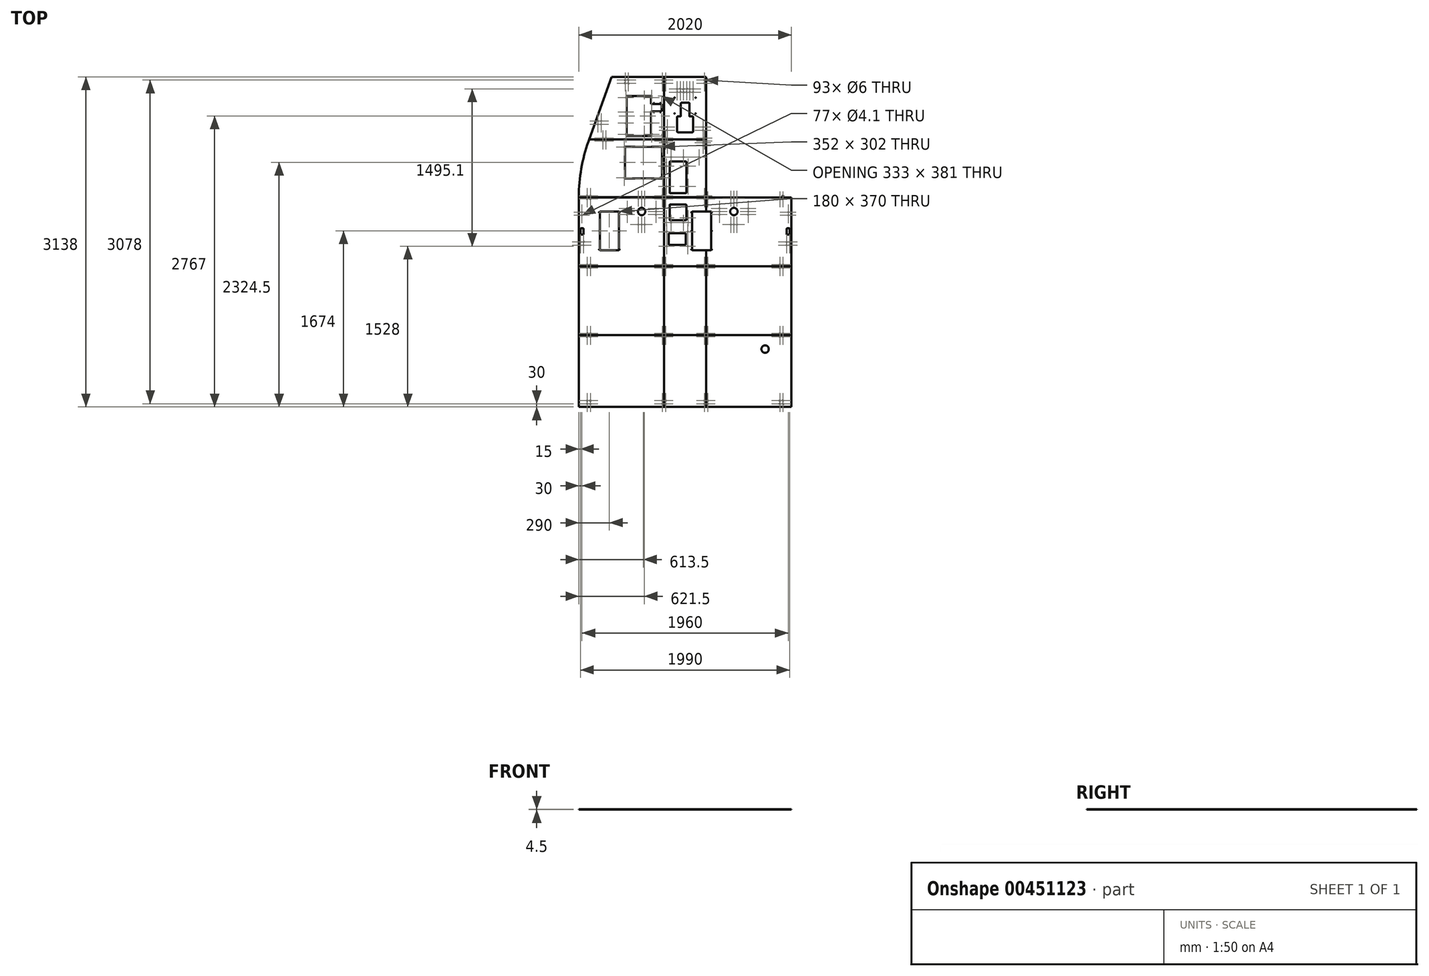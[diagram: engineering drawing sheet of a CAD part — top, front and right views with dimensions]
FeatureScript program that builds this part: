
annotation { "Feature Type Name" : "Feature", "Feature Type Description" : "" }
export const myFeature = defineFeature(function(context is Context, id is Id, definition is map)
    precondition{}
    {
        {
            var Q0;
            Q0=qCreatedBy(makeId("Top.planeOp"),FACE);
            var sketch = newSketch(context, id + "F0", { "sketchPlane" : qUnion([Q0])});
            skLineSegment(sketch, "E0.bottom", {"start": v(200, -327.5) * mm, "end": v(-200, -327.5) * mm});
            skLineSegment(sketch, "E0.top", {"start": v(200, 327.5) * mm, "end": v(-200, 327.5) * mm});
            skLineSegment(sketch, "E0.left", {"start": v(200, -327.5) * mm, "end": v(200, -176.5) * mm});
            skLineSegment(sketch, "E0.right", {"start": v(-200, -327.5) * mm, "end": v(-200, 327.5) * mm});
            skPoint(sketch, "E0.middle", {"position": v(0, 0) * mm});
            skCircle(sketch, "E1", {"center": v(185, 312.5) * mm, "radius": 3 * mm});
            skCircle(sketch, "E2", {"center": v(-185, 312.5) * mm, "radius": 3 * mm});
            skLineSegment(sketch, "E3.bottom", {"start": v(12.5, 109) * mm, "end": v(-147.5, 109) * mm});
            skLineSegment(sketch, "E3.top", {"start": v(12.5, 259) * mm, "end": v(-147.5, 259) * mm});
            skLineSegment(sketch, "E3.left", {"start": v(12.5, 109) * mm, "end": v(12.5, 259) * mm});
            skLineSegment(sketch, "E3.right", {"start": v(-147.5, 109) * mm, "end": v(-147.5, 259) * mm});
            skPoint(sketch, "E3.middle", {"position": v(-67.5, 184) * mm});
            skCircle(sketch, "E4", {"center": v(-134.5, 86.5) * mm, "radius": 2.05 * mm});
            skCircle(sketch, "E5", {"center": v(-17.5, 86.5) * mm, "radius": 2.05 * mm});
            skCircle(sketch, "E6", {"center": v(27.5, 131.5) * mm, "radius": 2.05 * mm});
            skCircle(sketch, "E7", {"center": v(-185, -312.5) * mm, "radius": 3 * mm});
            skCircle(sketch, "E8", {"center": v(185, -312.5) * mm, "radius": 3 * mm});
            skCircle(sketch, "E9", {"center": v(61, 185.5) * mm, "radius": 2.5 * mm});
            skCircle(sketch, "E10", {"center": v(61, 8.5) * mm, "radius": 2.5 * mm});
            skCircle(sketch, "E11", {"center": v(61, -168.5) * mm, "radius": 2.5 * mm});
            skLineSegment(sketch, "E12.bottom", {"start": v(200, -176.5) * mm, "end": v(67, -176.5) * mm});
            skLineSegment(sketch, "E12.top", {"start": v(200, 193.5) * mm, "end": v(67, 193.5) * mm});
            skLineSegment(sketch, "E12.right", {"start": v(67, -176.5) * mm, "end": v(67, 193.5) * mm});
            skPoint(sketch, "E12.middle", {"position": v(133.5, 8.5) * mm});
            skLineSegment(sketch, "E13.trimOffspring", {"start": v(200, 193.5) * mm, "end": v(200, 327.5) * mm});
            skLineSegment(sketch, "E14.bottom", {"start": v(5, -123.5) * mm, "end": v(-155, -123.5) * mm});
            skLineSegment(sketch, "E14.top", {"start": v(5, -13.5) * mm, "end": v(-155, -13.5) * mm});
            skLineSegment(sketch, "E14.left", {"start": v(5, -123.5) * mm, "end": v(5, -13.5) * mm});
            skLineSegment(sketch, "E14.right", {"start": v(-155, -123.5) * mm, "end": v(-155, -13.5) * mm});
            skPoint(sketch, "E14.middle", {"position": v(-75, -68.5) * mm});
            skCircle(sketch, "E15", {"center": v(-175, 0.5) * mm, "radius": 2.05 * mm});
            skCircle(sketch, "E16", {"center": v(-175, -137.5) * mm, "radius": 2.05 * mm});
            skCircle(sketch, "E17", {"center": v(25, 0.5) * mm, "radius": 2.05 * mm});
            skCircle(sketch, "E18", {"center": v(25, -137.5) * mm, "radius": 2.05 * mm});
            skCircle(sketch, "E19", {"center": v(-177.5, 131.5) * mm, "radius": 2.05 * mm});
            skSolve(sketch);
        }
        {
            var Q0;
            Q0=qSketchRegion(id+"F0",true);
            extrude(context, id + "F1", {"entities" : qUnion([Q0]), "depth" : 4.5 * mm, "offsetDistance" : 25 * mm});
        }
        {
            var Q0;
            Q0=qCreatedBy(makeId("Top.planeOp"),FACE);
            var sketch = newSketch(context, id + "F2", { "sketchPlane" : qUnion([Q0])});
            skLineSegment(sketch, "E20.top", {"start": v(-200, 877.5) * mm, "end": v(-912, 877.5) * mm});
            skLineSegment(sketch, "E20.left", {"start": v(-200, 327.5) * mm, "end": v(-200, 877.5) * mm});
            skPoint(sketch, "E20.middle", {"position": v(-556, 602.5) * mm});
            skLineSegment(sketch, "E21", {"start": v(-200, 327.5) * mm, "end": v(-1010, 327.5) * mm});
            skCircle(sketch, "E22", {"center": v(-215, 862.5) * mm, "radius": 3 * mm});
            skCircle(sketch, "E23", {"center": v(-215, 342.5) * mm, "radius": 3 * mm});
            skCircle(sketch, "E24", {"center": v(-930, 342.5) * mm, "radius": 3 * mm});
            skCircle(sketch, "E25", {"center": v(-782, 862.5) * mm, "radius": 3 * mm});
            skLineSegment(sketch, "E26.left", {"start": v(-200, 877.5) * mm, "end": v(-200, 1472.5) * mm});
            skPoint(sketch, "E26.middle", {"position": v(-556, 1175) * mm});
            skLineSegment(sketch, "E27", {"start": v(-200, 1472.5) * mm, "end": v(-700, 1472.5) * mm});
            skLineSegment(sketch, "E28", {"start": v(-912, 877.5) * mm, "end": v(-700, 1472.5) * mm});
            skCircle(sketch, "E29", {"center": v(-215, 1442.5) * mm, "radius": 3 * mm});
            skCircle(sketch, "E30", {"center": v(-215, 892.5) * mm, "radius": 3 * mm});
            skCircle(sketch, "E31", {"center": v(-782, 892.5) * mm, "radius": 3 * mm});
            skCircle(sketch, "E32", {"center": v(-570, 1442.5) * mm, "radius": 3 * mm});
            skLineSegment(sketch, "E33", {"start": v(0, 1490.85) * mm, "end": v(0, 501.43) * mm, "construction": true});
            skCircle(sketch, "E34.MirrorC", {"center": v(215, 1442.5) * mm, "radius": 3 * mm});
            skCircle(sketch, "E35.MirrorC", {"center": v(930, 342.5) * mm, "radius": 3 * mm});
            skCircle(sketch, "E36.MirrorC", {"center": v(782, 862.5) * mm, "radius": 3 * mm});
            skCircle(sketch, "E37.MirrorC", {"center": v(782, 892.5) * mm, "radius": 3 * mm});
            skCircle(sketch, "E38.MirrorC", {"center": v(570, 1442.5) * mm, "radius": 3 * mm});
            skCircle(sketch, "E39.MirrorC", {"center": v(215, 862.5) * mm, "radius": 3 * mm});
            skCircle(sketch, "E40.MirrorC", {"center": v(215, 342.5) * mm, "radius": 3 * mm});
            skCircle(sketch, "E41.MirrorC", {"center": v(215, 892.5) * mm, "radius": 3 * mm});
            skLineSegment(sketch, "E42.MirrorCS", {"start": v(200, 1472.5) * mm, "end": v(700, 1472.5) * mm});
            skLineSegment(sketch, "E43.MirrorCS", {"start": v(1010, 327.5) * mm, "end": v(912, 877.5) * mm, "construction": true});
            skLineSegment(sketch, "E44.MirrorCS", {"start": v(200, 877.5) * mm, "end": v(912, 877.5) * mm});
            skPoint(sketch, "E45.MirrorP", {"position": v(556, 1175) * mm});
            skLineSegment(sketch, "E46.MirrorCS", {"start": v(200, 327.5) * mm, "end": v(200, 877.5) * mm});
            skPoint(sketch, "E47.MirrorP", {"position": v(556, 602.5) * mm});
            skLineSegment(sketch, "E48.MirrorCS", {"start": v(200, 327.5) * mm, "end": v(1010, 327.5) * mm});
            skLineSegment(sketch, "E49.MirrorCS", {"start": v(912, 877.5) * mm, "end": v(700, 1472.5) * mm});
            skLineSegment(sketch, "E50.MirrorCS", {"start": v(200, 877.5) * mm, "end": v(200, 1472.5) * mm});
            skCircle(sketch, "E51", {"center": v(-900, 342.5) * mm, "radius": 3 * mm});
            skCircle(sketch, "E52", {"center": v(-752, 862.5) * mm, "radius": 3 * mm});
            skCircle(sketch, "E53", {"center": v(-752, 892.5) * mm, "radius": 3 * mm});
            skCircle(sketch, "E54", {"center": v(-570, 1412.5) * mm, "radius": 3 * mm});
            skCircle(sketch, "E55", {"center": v(-540, 1442.5) * mm, "radius": 3 * mm});
            skCircle(sketch, "E56", {"center": v(-540, 1412.5) * mm, "radius": 3 * mm});
            skCircle(sketch, "E57", {"center": v(-215, 1412.5) * mm, "radius": 3 * mm});
            skCircle(sketch, "E58.MirrorC", {"center": v(215, 1412.5) * mm, "radius": 3 * mm});
            skCircle(sketch, "E59.MirrorC", {"center": v(540, 1442.5) * mm, "radius": 3 * mm});
            skCircle(sketch, "E60.MirrorC", {"center": v(540, 1412.5) * mm, "radius": 3 * mm});
            skCircle(sketch, "E61.MirrorC", {"center": v(570, 1412.5) * mm, "radius": 3 * mm});
            skCircle(sketch, "E62.MirrorC", {"center": v(752, 892.5) * mm, "radius": 3 * mm});
            skCircle(sketch, "E63.MirrorC", {"center": v(752, 862.5) * mm, "radius": 3 * mm});
            skCircle(sketch, "E64.MirrorC", {"center": v(900, 342.5) * mm, "radius": 3 * mm});
            skCircle(sketch, "E65", {"center": v(-828.5, 1052.5) * mm, "radius": 2.05 * mm});
            skCircle(sketch, "E66", {"center": v(-798.5, 1052.5) * mm, "radius": 2.05 * mm});
            skCircle(sketch, "E67", {"center": v(-828.5, 1022.5) * mm, "radius": 2.05 * mm});
            skCircle(sketch, "E68", {"center": v(-798.5, 1022.5) * mm, "radius": 2.05 * mm});
            skCircle(sketch, "E69.MirrorC", {"center": v(828.5, 1022.5) * mm, "radius": 2.05 * mm});
            skCircle(sketch, "E70.MirrorC", {"center": v(798.5, 1052.5) * mm, "radius": 2.05 * mm});
            skCircle(sketch, "E71.MirrorC", {"center": v(828.5, 1052.5) * mm, "radius": 2.05 * mm});
            skCircle(sketch, "E72.MirrorC", {"center": v(798.5, 1022.5) * mm, "radius": 2.05 * mm});
            skCircle(sketch, "E73", {"center": v(-443.5, 383.5) * mm, "radius": 2.05 * mm, "construction": true});
            skCircle(sketch, "E74", {"center": v(-413.5, 383.5) * mm, "radius": 2.05 * mm, "construction": true});
            skCircle(sketch, "E75", {"center": v(-383.5, 383.5) * mm, "radius": 2.05 * mm, "construction": true});
            skCircle(sketch, "E76", {"center": v(433.5, 383.5) * mm, "radius": 2.05 * mm, "construction": true});
            skCircle(sketch, "E77", {"center": v(463.5, 383.5) * mm, "radius": 2.05 * mm, "construction": true});
            skCircle(sketch, "E78", {"center": v(493.5, 383.5) * mm, "radius": 2.05 * mm, "construction": true});
            skLineSegment(sketch, "E79", {"start": v(-912, 877.5) * mm, "end": v(-918.71, 858.66) * mm});
            skLineSegment(sketch, "E80", {"start": v(-1010, 327.5) * mm, "end": v(-1010, 347.5) * mm});
            skArc(sketch, "E81", {"start": v(-918.71, 858.66) * mm, "mid": v(-987.26, 597.02) * mm, "end": v(-1010, 327.5) * mm});
            skLineSegment(sketch, "E82.MirrorCS", {"start": v(912, 877.5) * mm, "end": v(918.71, 858.66) * mm});
            skArc(sketch, "E83.MirrorCS", {"start": v(918.71, 858.66) * mm, "mid": v(987.26, 597.02) * mm, "end": v(1010, 327.5) * mm});
            skLineSegment(sketch, "E84", {"start": v(362.89, 612.5) * mm, "end": v(500.57, 612.5) * mm, "construction": true});
            skLineSegment(sketch, "E85", {"start": v(428.5, 713.45) * mm, "end": v(428.5, 506) * mm, "construction": true});
            skCircle(sketch, "E86", {"center": v(428.5, 612.5) * mm, "radius": 44.04 * mm, "construction": true});
            skCircle(sketch, "E87", {"center": v(472, 816) * mm, "radius": 2.05 * mm});
            skCircle(sketch, "E88", {"center": v(290, 804) * mm, "radius": 2.05 * mm});
            skCircle(sketch, "E89", {"center": v(654, 804) * mm, "radius": 2.05 * mm});
            skCircle(sketch, "E90", {"center": v(290, 514) * mm, "radius": 2.05 * mm});
            skCircle(sketch, "E91", {"center": v(654, 514) * mm, "radius": 2.05 * mm});
            skCircle(sketch, "E92", {"center": v(472, 502) * mm, "radius": 2.05 * mm});
            skLineSegment(sketch, "E93.bottom", {"start": v(648, 508) * mm, "end": v(296, 508) * mm});
            skLineSegment(sketch, "E93.top", {"start": v(648, 810) * mm, "end": v(296, 810) * mm});
            skLineSegment(sketch, "E93.left", {"start": v(648, 508) * mm, "end": v(648, 810) * mm});
            skLineSegment(sketch, "E93.right", {"start": v(296, 508) * mm, "end": v(296, 810) * mm});
            skPoint(sketch, "E93.middle", {"position": v(472, 659) * mm});
            skCircle(sketch, "E94", {"center": v(-440, 612.5) * mm, "radius": 49.26 * mm, "construction": true});
            skLineSegment(sketch, "E95.bottom", {"start": v(-220.5, 508) * mm, "end": v(-572.5, 508) * mm});
            skLineSegment(sketch, "E95.top", {"start": v(-220.5, 810) * mm, "end": v(-572.5, 810) * mm});
            skLineSegment(sketch, "E95.left", {"start": v(-220.5, 508) * mm, "end": v(-220.5, 810) * mm});
            skLineSegment(sketch, "E95.right", {"start": v(-572.5, 508) * mm, "end": v(-572.5, 810) * mm});
            skPoint(sketch, "E95.middle", {"position": v(-396.5, 659) * mm});
            skCircle(sketch, "E96", {"center": v(-396.5, 816) * mm, "radius": 2.05 * mm});
            skCircle(sketch, "E97", {"center": v(-578.5, 804) * mm, "radius": 2.05 * mm});
            skCircle(sketch, "E98", {"center": v(-214.5, 804) * mm, "radius": 2.05 * mm});
            skCircle(sketch, "E99", {"center": v(-578.5, 514) * mm, "radius": 2.05 * mm});
            skCircle(sketch, "E100", {"center": v(-214.5, 514) * mm, "radius": 2.05 * mm});
            skCircle(sketch, "E101", {"center": v(-396.5, 502) * mm, "radius": 2.05 * mm});
            skCircle(sketch, "E102", {"center": v(306.5, 927.5) * mm, "radius": 2.05 * mm});
            skCircle(sketch, "E103", {"center": v(306.5, 1033.5) * mm, "radius": 2.05 * mm});
            skCircle(sketch, "E104", {"center": v(306.5, 1139.5) * mm, "radius": 2.05 * mm});
            skCircle(sketch, "E105", {"center": v(306.5, 1275.5) * mm, "radius": 2.05 * mm});
            skLineSegment(sketch, "E106", {"start": v(428.5, 1020.14) * mm, "end": v(428.5, 1253.54) * mm, "construction": true});
            skCircle(sketch, "E107.MirrorC", {"center": v(550.5, 1275.5) * mm, "radius": 2.05 * mm});
            skCircle(sketch, "E108.MirrorC", {"center": v(550.5, 1139.5) * mm, "radius": 2.05 * mm});
            skCircle(sketch, "E109.MirrorC", {"center": v(550.5, 1033.5) * mm, "radius": 2.05 * mm});
            skCircle(sketch, "E110.MirrorC", {"center": v(550.5, 927.5) * mm, "radius": 2.05 * mm});
            skLineSegment(sketch, "E111.bottom", {"start": v(543.5, 911) * mm, "end": v(313.5, 911) * mm});
            skLineSegment(sketch, "E111.top", {"start": v(543.5, 1292) * mm, "end": v(313.5, 1292) * mm});
            skLineSegment(sketch, "E111.left", {"start": v(543.5, 911) * mm, "end": v(543.5, 1292) * mm});
            skLineSegment(sketch, "E111.right", {"start": v(313.5, 911) * mm, "end": v(313.5, 1292) * mm});
            skPoint(sketch, "E111.middle", {"position": v(428.5, 1101.5) * mm});
            skLineSegment(sketch, "E112", {"start": v(622.25, 908.7) * mm, "end": v(655.12, 908.7) * mm, "construction": true});
            skLineSegment(sketch, "E113", {"start": v(640.84, 1294.3) * mm, "end": v(669.73, 1294.3) * mm, "construction": true});
            skPoint(sketch, "E114", {"position": v(655.28, 1101.5) * mm});
            skPoint(sketch, "E114.positionSnap0", {"position": v(655.28, 1294.3) * mm});
            skLineSegment(sketch, "E115", {"start": v(543.5, 1215.5) * mm, "end": v(646.5, 1215.5) * mm});
            skLineSegment(sketch, "E116", {"start": v(646.5, 1215.5) * mm, "end": v(646.5, 1145.5) * mm});
            skLineSegment(sketch, "E117", {"start": v(646.5, 1145.5) * mm, "end": v(543.5, 1145.5) * mm});
            skLineSegment(sketch, "E118.MirrorCS", {"start": v(313.5, 911) * mm, "end": v(543.5, 911) * mm});
            skLineSegment(sketch, "E119.MirrorCS", {"start": v(313.5, 1292) * mm, "end": v(543.5, 1292) * mm});
            skCircle(sketch, "E120", {"center": v(573.5, 1222.5) * mm, "radius": 2.5 * mm});
            skCircle(sketch, "E121", {"center": v(633.5, 1222.5) * mm, "radius": 2.5 * mm});
            skCircle(sketch, "E122", {"center": v(573.5, 1138.5) * mm, "radius": 2.5 * mm});
            skCircle(sketch, "E123", {"center": v(633.5, 1138.5) * mm, "radius": 2.5 * mm});
            skLineSegment(sketch, "E124", {"start": v(-5, 1141.85) * mm, "end": v(-5, 1115.7) * mm, "construction": true});
            skCircle(sketch, "E125.MirrorC", {"center": v(-318, 1275.5) * mm, "radius": 2.05 * mm});
            skCircle(sketch, "E126.MirrorC", {"center": v(-562, 1275.5) * mm, "radius": 2.05 * mm});
            skCircle(sketch, "E127.MirrorC", {"center": v(-318, 927.5) * mm, "radius": 2.05 * mm});
            skCircle(sketch, "E128.MirrorC", {"center": v(-562, 1139.5) * mm, "radius": 2.05 * mm});
            skCircle(sketch, "E129.MirrorC", {"center": v(-562, 927.5) * mm, "radius": 2.05 * mm});
            skCircle(sketch, "E130.MirrorC", {"center": v(-318, 1139.5) * mm, "radius": 2.05 * mm});
            skCircle(sketch, "E131.MirrorC", {"center": v(-562, 1033.5) * mm, "radius": 2.05 * mm});
            skCircle(sketch, "E132.MirrorC", {"center": v(-318, 1033.5) * mm, "radius": 2.05 * mm});
            skPoint(sketch, "E133.MirrorP", {"position": v(-440, 1101.5) * mm});
            skLineSegment(sketch, "E134", {"start": v(-325, 1215.5) * mm, "end": v(-222, 1215.5) * mm});
            skLineSegment(sketch, "E135", {"start": v(-222, 1215.5) * mm, "end": v(-222, 1145.5) * mm});
            skLineSegment(sketch, "E136", {"start": v(-222, 1145.5) * mm, "end": v(-325, 1145.5) * mm});
            skCircle(sketch, "E137", {"center": v(-295, 1222.5) * mm, "radius": 2.5 * mm});
            skCircle(sketch, "E138", {"center": v(-235, 1222.5) * mm, "radius": 2.5 * mm});
            skCircle(sketch, "E139", {"center": v(-295, 1138.5) * mm, "radius": 2.5 * mm});
            skCircle(sketch, "E140", {"center": v(-235, 1138.5) * mm, "radius": 2.5 * mm});
            skLineSegment(sketch, "E141.bottom", {"start": v(-325, 911) * mm, "end": v(-555, 911) * mm});
            skLineSegment(sketch, "E141.top", {"start": v(-325, 1292) * mm, "end": v(-555, 1292) * mm});
            skLineSegment(sketch, "E141.left", {"start": v(-325, 911) * mm, "end": v(-325, 1292) * mm});
            skLineSegment(sketch, "E141.right", {"start": v(-555, 911) * mm, "end": v(-555, 1292) * mm});
            skSolve(sketch);
        }
        {
            var Q0;
            Q0=makeQuery(id+"F2.imprint","IMPRINT",FACE,{"disambiguationData":[TD([[makeQuery(id+"F2.imprint","IMPRINT",EDGE,{"derivedFrom":sQuery(id+"F2.wireOp",EDGE,"E20.left")}),1.0]])]});
            var Q1;
            Q1=makeQuery(id+"F2.imprint","IMPRINT",FACE,{"disambiguationData":[TD([[makeQuery(id+"F2.imprint","IMPRINT",EDGE,{"derivedFrom":sQuery(id+"F2.wireOp",EDGE,"E35.MirrorC")}),1.0]])]});
            extrude(context, id + "F3", {"entities" : qUnion([Q0, Q1]), "depth" : 4.5 * mm, "offsetDistance" : 25 * mm});
        }
        {
            var Q0;
            Q0=makeQuery(id+"F2.imprint","IMPRINT",FACE,{"disambiguationData":[TD([[makeQuery(id+"F2.imprint","IMPRINT",EDGE,{"derivedFrom":sQuery(id+"F2.wireOp",EDGE,"E20.top")}),-1.0]])]});
            var Q1;
            Q1=makeQuery(id+"F2.imprint","IMPRINT",FACE,{"disambiguationData":[TD([[makeQuery(id+"F2.imprint","IMPRINT",EDGE,{"derivedFrom":sQuery(id+"F2.wireOp",EDGE,"E34.MirrorC")}),1.0]])]});
            extrude(context, id + "F4", {"entities" : qUnion([Q0, Q1]), "depth" : 4.5 * mm, "offsetDistance" : 25 * mm});
        }
        {
            var Q0;
            Q0=qCreatedBy(makeId("Top.planeOp"),FACE);
            var sketch = newSketch(context, id + "F5", { "sketchPlane" : qUnion([Q0])});
            skLineSegment(sketch, "E142.bottom", {"start": v(200, 877.5) * mm, "end": v(-200, 877.5) * mm});
            skLineSegment(sketch, "E142.top", {"start": v(200, 327.5) * mm, "end": v(-200, 327.5) * mm});
            skLineSegment(sketch, "E142.left", {"start": v(200, 877.5) * mm, "end": v(200, 327.5) * mm});
            skLineSegment(sketch, "E142.right", {"start": v(-200, 877.5) * mm, "end": v(-200, 327.5) * mm});
            skPoint(sketch, "E142.middle", {"position": v(0, 602.5) * mm});
            skCircle(sketch, "E143", {"center": v(-132.5, 709.1) * mm, "radius": 2.05 * mm});
            skCircle(sketch, "E144", {"center": v(-17.5, 709.1) * mm, "radius": 2.05 * mm});
            skCircle(sketch, "E145", {"center": v(132.5, 709.1) * mm, "radius": 2.05 * mm});
            skCircle(sketch, "E146", {"center": v(-185, 862.5) * mm, "radius": 3 * mm});
            skCircle(sketch, "E147", {"center": v(185, 862.5) * mm, "radius": 3 * mm});
            skCircle(sketch, "E148", {"center": v(-185, 342.5) * mm, "radius": 3 * mm});
            skCircle(sketch, "E149", {"center": v(185, 342.5) * mm, "radius": 3 * mm});
            skCircle(sketch, "E150", {"center": v(170, 847.5) * mm, "radius": 2.05 * mm});
            skCircle(sketch, "E151", {"center": v(170, 817.5) * mm, "radius": 2.05 * mm});
            skLineSegment(sketch, "E152", {"start": v(0, 602.5) * mm, "end": v(0, 499.57) * mm, "construction": true});
            skCircle(sketch, "E153.MirrorC", {"center": v(-170, 817.5) * mm, "radius": 2.05 * mm});
            skCircle(sketch, "E154.MirrorC", {"center": v(-170, 847.5) * mm, "radius": 2.05 * mm});
            skLineSegment(sketch, "E155.bottom", {"start": v(12.5, 367.5) * mm, "end": v(-147.5, 367.5) * mm});
            skLineSegment(sketch, "E155.top", {"start": v(12.5, 667.5) * mm, "end": v(-147.5, 667.5) * mm});
            skLineSegment(sketch, "E155.left", {"start": v(12.5, 367.5) * mm, "end": v(12.5, 667.5) * mm});
            skLineSegment(sketch, "E155.right", {"start": v(-147.5, 367.5) * mm, "end": v(-147.5, 667.5) * mm});
            skPoint(sketch, "E155.middle", {"position": v(-67.5, 517.5) * mm});
            skCircle(sketch, "E156", {"center": v(-177.5, 431.5) * mm, "radius": 2.05 * mm});
            skCircle(sketch, "E157", {"center": v(27.5, 431.5) * mm, "radius": 2.05 * mm});
            skCircle(sketch, "E158", {"center": v(-177.5, 624.1) * mm, "radius": 2.05 * mm});
            skCircle(sketch, "E159", {"center": v(27.5, 624.1) * mm, "radius": 2.05 * mm});
            skSolve(sketch);
        }
        {
            var Q0;
            Q0=qSketchRegion(id+"F5",true);
            extrude(context, id + "F6", {"entities" : qUnion([Q0]), "depth" : 4.5 * mm, "offsetDistance" : 25 * mm});
        }
        {
            var Q0;
            Q0=qCreatedBy(makeId("Top.planeOp"),FACE);
            var sketch = newSketch(context, id + "F7", { "sketchPlane" : qUnion([Q0])});
            skLineSegment(sketch, "E160.bottom", {"start": v(-200, 877.5) * mm, "end": v(200, 877.5) * mm});
            skLineSegment(sketch, "E160.top", {"start": v(200, 1472.5) * mm, "end": v(-200, 1472.5) * mm});
            skLineSegment(sketch, "E160.left", {"start": v(-200, 877.5) * mm, "end": v(-200, 1472.5) * mm});
            skLineSegment(sketch, "E160.right", {"start": v(200, 877.5) * mm, "end": v(200, 1472.5) * mm});
            skPoint(sketch, "E160.middle", {"position": v(0, 1175) * mm});
            skCircle(sketch, "E161", {"center": v(170, 947.5) * mm, "radius": 2.05 * mm, "construction": true});
            skCircle(sketch, "E162", {"center": v(170, 917.5) * mm, "radius": 2.05 * mm, "construction": true});
            skCircle(sketch, "E163", {"center": v(170, 965.5) * mm, "radius": 2.05 * mm});
            skCircle(sketch, "E164", {"center": v(170, 995.5) * mm, "radius": 2.05 * mm});
            skCircle(sketch, "E165.MirrorC", {"center": v(-170, 947.5) * mm, "radius": 2.05 * mm, "construction": true});
            skCircle(sketch, "E166.MirrorC", {"center": v(-170, 965.5) * mm, "radius": 2.05 * mm});
            skCircle(sketch, "E167.MirrorC", {"center": v(-170, 995.5) * mm, "radius": 2.05 * mm});
            skCircle(sketch, "E168.MirrorC", {"center": v(-170, 917.5) * mm, "radius": 2.05 * mm, "construction": true});
            skCircle(sketch, "E169", {"center": v(185, 1442.5) * mm, "radius": 3 * mm});
            skCircle(sketch, "E170", {"center": v(-185, 1442.5) * mm, "radius": 3 * mm});
            skCircle(sketch, "E171", {"center": v(185, 892.5) * mm, "radius": 3 * mm});
            skCircle(sketch, "E172", {"center": v(-185, 892.5) * mm, "radius": 3 * mm});
            skCircle(sketch, "E173", {"center": v(-185, 1412.5) * mm, "radius": 3 * mm});
            skCircle(sketch, "E174", {"center": v(185, 1412.5) * mm, "radius": 3 * mm});
            skLineSegment(sketch, "E175.bottom", {"start": v(75, 946.5) * mm, "end": v(-75, 946.5) * mm});
            skLineSegment(sketch, "E175.top", {"start": v(75, 1096.5) * mm, "end": v(-75, 1096.5) * mm});
            skLineSegment(sketch, "E175.left", {"start": v(75, 946.5) * mm, "end": v(75, 1096.5) * mm});
            skLineSegment(sketch, "E175.right", {"start": v(-75, 946.5) * mm, "end": v(-75, 1096.5) * mm});
            skPoint(sketch, "E175.middle", {"position": v(0, 1021.5) * mm});
            skCircle(sketch, "E176", {"center": v(-15, 1457.5) * mm, "radius": 3 * mm, "construction": true});
            skCircle(sketch, "E177", {"center": v(15, 1457.5) * mm, "radius": 3 * mm, "construction": true});
            skCircle(sketch, "E178", {"center": v(-15, 1427.5) * mm, "radius": 3 * mm, "construction": true});
            skCircle(sketch, "E179", {"center": v(15, 1427.5) * mm, "radius": 3 * mm, "construction": true});
            skCircle(sketch, "E180", {"center": v(-45, 1357.6) * mm, "radius": 2.05 * mm});
            skCircle(sketch, "E181", {"center": v(-45, 1327.6) * mm, "radius": 2.05 * mm});
            skCircle(sketch, "E182", {"center": v(45, 1357.6) * mm, "radius": 2.05 * mm});
            skCircle(sketch, "E183", {"center": v(45, 1327.6) * mm, "radius": 2.05 * mm});
            skLineSegment(sketch, "E184", {"start": v(-30, 1503.65) * mm, "end": v(-30, 1424.1) * mm, "construction": true});
            skLineSegment(sketch, "E185", {"start": v(30, 1481.15) * mm, "end": v(30, 1393.6) * mm, "construction": true});
            skCircle(sketch, "E186", {"center": v(-75, 1357.6) * mm, "radius": 2.05 * mm});
            skCircle(sketch, "E187", {"center": v(-75, 1327.6) * mm, "radius": 2.05 * mm});
            skLineSegment(sketch, "E188", {"start": v(0, 1346.91) * mm, "end": v(0, 1586.58) * mm, "construction": true});
            skPoint(sketch, "E188.endSnap0", {"position": v(0, 1472.5) * mm});
            skCircle(sketch, "E189.MirrorC", {"center": v(75, 1327.6) * mm, "radius": 2.05 * mm});
            skCircle(sketch, "E190.MirrorC", {"center": v(75, 1357.6) * mm, "radius": 2.05 * mm});
            skCircle(sketch, "E191", {"center": v(-15, 1357.6) * mm, "radius": 3 * mm});
            skCircle(sketch, "E192", {"center": v(15, 1357.6) * mm, "radius": 3 * mm});
            skCircle(sketch, "E193", {"center": v(-15, 1327.6) * mm, "radius": 3 * mm});
            skCircle(sketch, "E194", {"center": v(15, 1327.6) * mm, "radius": 3 * mm});
            skLineSegment(sketch, "E195", {"start": v(-24.25, 1372.6) * mm, "end": v(29.76, 1372.6) * mm, "construction": true});
            skCircle(sketch, "E196", {"center": v(-100, 1275) * mm, "radius": 2.5 * mm});
            skCircle(sketch, "E197", {"center": v(100, 1275) * mm, "radius": 2.5 * mm});
            skCircle(sketch, "E198", {"center": v(-100, 1125) * mm, "radius": 2.5 * mm});
            skCircle(sketch, "E199", {"center": v(100, 1125) * mm, "radius": 2.5 * mm});
            skLineSegment(sketch, "E200", {"start": v(-40, 1096.5) * mm, "end": v(-40, 1226.5) * mm});
            skLineSegment(sketch, "E201", {"start": v(-40, 1226.5) * mm, "end": v(40, 1226.5) * mm});
            skLineSegment(sketch, "E202", {"start": v(40, 1226.5) * mm, "end": v(40, 1096.5) * mm});
            skSolve(sketch);
        }
        {
            var Q0;
            Q0=qSketchRegion(id+"F7",true);
            extrude(context, id + "F8", {"entities" : qUnion([Q0]), "depth" : 4.5 * mm, "offsetDistance" : 25 * mm});
        }
        {
            var Q0;
            Q0=qCreatedBy(makeId("Top.planeOp"),FACE);
            var sketch = newSketch(context, id + "F9", { "sketchPlane" : qUnion([Q0])});
            skLineSegment(sketch, "E203.bottom", {"start": v(-200, -327.5) * mm, "end": v(-1010, -327.5) * mm});
            skLineSegment(sketch, "E203.top", {"start": v(-200, 327.5) * mm, "end": v(-1010, 327.5) * mm});
            skLineSegment(sketch, "E203.left", {"start": v(-200, -327.5) * mm, "end": v(-200, 327.5) * mm});
            skLineSegment(sketch, "E203.right", {"start": v(-1010, -327.5) * mm, "end": v(-1010, 327.5) * mm});
            skPoint(sketch, "E203.middle", {"position": v(-605, 0) * mm});
            skPoint(sketch, "E204", {"position": v(-930, 312.5) * mm});
            skPoint(sketch, "E205", {"position": v(-215, 312.5) * mm});
            skPoint(sketch, "E206", {"position": v(-930, -312.5) * mm});
            skPoint(sketch, "E207", {"position": v(-215, -312.5) * mm});
            skCircle(sketch, "E208", {"center": v(-930, 312.5) * mm, "radius": 3 * mm});
            skCircle(sketch, "E209", {"center": v(-215, 312.5) * mm, "radius": 3 * mm});
            skCircle(sketch, "E210", {"center": v(-930, -312.5) * mm, "radius": 3 * mm});
            skCircle(sketch, "E211", {"center": v(-215, -312.5) * mm, "radius": 3 * mm});
            skLineSegment(sketch, "E212.bottom", {"start": v(200, -327.5) * mm, "end": v(1010, -327.5) * mm});
            skLineSegment(sketch, "E212.top", {"start": v(200, 327.5) * mm, "end": v(1010, 327.5) * mm});
            skLineSegment(sketch, "E212.left", {"start": v(200, -327.5) * mm, "end": v(200, -176.5) * mm});
            skLineSegment(sketch, "E212.right", {"start": v(1010, -327.5) * mm, "end": v(1010, 327.5) * mm});
            skPoint(sketch, "E212.middle", {"position": v(605, 0) * mm});
            skCircle(sketch, "E213", {"center": v(215, 312.5) * mm, "radius": 3 * mm});
            skCircle(sketch, "E214", {"center": v(930, 312.5) * mm, "radius": 3 * mm});
            skCircle(sketch, "E215", {"center": v(215, -312.5) * mm, "radius": 3 * mm});
            skCircle(sketch, "E216", {"center": v(930, -312.5) * mm, "radius": 3 * mm});
            skCircle(sketch, "E217", {"center": v(-900, -312.5) * mm, "radius": 3 * mm});
            skCircle(sketch, "E218", {"center": v(-900, 312.5) * mm, "radius": 3 * mm});
            skCircle(sketch, "E219", {"center": v(900, -312.5) * mm, "radius": 3 * mm});
            skCircle(sketch, "E220", {"center": v(900, 312.5) * mm, "radius": 3 * mm});
            skCircle(sketch, "E221", {"center": v(-995, -97.5) * mm, "radius": 3 * mm});
            skCircle(sketch, "E222", {"center": v(-965, -97.5) * mm, "radius": 3 * mm});
            skCircle(sketch, "E223", {"center": v(-995, -127.5) * mm, "radius": 3 * mm});
            skCircle(sketch, "E224", {"center": v(-965, -127.5) * mm, "radius": 3 * mm});
            skCircle(sketch, "E225", {"center": v(995, -97.5) * mm, "radius": 3 * mm});
            skCircle(sketch, "E226", {"center": v(965, -97.5) * mm, "radius": 3 * mm});
            skCircle(sketch, "E227", {"center": v(965, -127.5) * mm, "radius": 3 * mm});
            skCircle(sketch, "E228", {"center": v(995, -127.5) * mm, "radius": 3 * mm});
            skCircle(sketch, "E229", {"center": v(601, 222.5) * mm, "radius": 2.05 * mm});
            skCircle(sketch, "E230", {"center": v(601, 192.5) * mm, "radius": 2.05 * mm});
            skCircle(sketch, "E231", {"center": v(601, 162.5) * mm, "radius": 2.05 * mm});
            skCircle(sketch, "E232", {"center": v(326, 222.5) * mm, "radius": 2.05 * mm});
            skCircle(sketch, "E233", {"center": v(326, 192.5) * mm, "radius": 2.05 * mm});
            skCircle(sketch, "E234", {"center": v(326, 162.5) * mm, "radius": 2.05 * mm});
            skLineSegment(sketch, "E235", {"start": v(0, -608.3) * mm, "end": v(0, 1601.34) * mm, "construction": true});
            skCircle(sketch, "E236", {"center": v(-276, 222.5) * mm, "radius": 2.05 * mm});
            skCircle(sketch, "E237", {"center": v(-276, 192.5) * mm, "radius": 2.05 * mm});
            skCircle(sketch, "E238", {"center": v(-276, 162.5) * mm, "radius": 2.05 * mm});
            skCircle(sketch, "E239", {"center": v(-551, 222.5) * mm, "radius": 2.05 * mm});
            skCircle(sketch, "E240", {"center": v(-551, 192.5) * mm, "radius": 2.05 * mm});
            skCircle(sketch, "E241", {"center": v(-551, 162.5) * mm, "radius": 2.05 * mm});
            skCircle(sketch, "E242", {"center": v(433.5, 67.5) * mm, "radius": 2.05 * mm});
            skCircle(sketch, "E243", {"center": v(463.5, 67.5) * mm, "radius": 2.05 * mm});
            skCircle(sketch, "E244", {"center": v(493.5, 67.5) * mm, "radius": 2.05 * mm});
            skCircle(sketch, "E245", {"center": v(-443.5, 67.5) * mm, "radius": 2.05 * mm});
            skCircle(sketch, "E246", {"center": v(-413.5, 67.5) * mm, "radius": 2.05 * mm});
            skCircle(sketch, "E247", {"center": v(-383.5, 67.5) * mm, "radius": 2.05 * mm});
            skCircle(sketch, "E248", {"center": v(980, 187.5) * mm, "radius": 2.05 * mm});
            skCircle(sketch, "E249", {"center": v(980, 157.5) * mm, "radius": 2.05 * mm});
            skCircle(sketch, "E250.MirrorC", {"center": v(-980, 157.5) * mm, "radius": 2.05 * mm});
            skCircle(sketch, "E251.MirrorC", {"center": v(-980, 187.5) * mm, "radius": 2.05 * mm});
            skCircle(sketch, "E252", {"center": v(253, 185.5) * mm, "radius": 2.5 * mm});
            skCircle(sketch, "E253", {"center": v(253, 8.5) * mm, "radius": 2.5 * mm});
            skCircle(sketch, "E254", {"center": v(253, -168.5) * mm, "radius": 2.5 * mm});
            skCircle(sketch, "E255", {"center": v(-624, 185.5) * mm, "radius": 2.5 * mm});
            skCircle(sketch, "E256", {"center": v(-624, 8.5) * mm, "radius": 2.5 * mm});
            skCircle(sketch, "E257", {"center": v(-624, -168.5) * mm, "radius": 2.5 * mm});
            skCircle(sketch, "E258", {"center": v(-816, 185.5) * mm, "radius": 2.5 * mm});
            skCircle(sketch, "E259", {"center": v(-816, 8.5) * mm, "radius": 2.5 * mm});
            skCircle(sketch, "E260", {"center": v(-816, -168.5) * mm, "radius": 2.5 * mm});
            skLineSegment(sketch, "E261.bottom", {"start": v(-630, -176.5) * mm, "end": v(-810, -176.5) * mm});
            skLineSegment(sketch, "E261.top", {"start": v(-630, 193.5) * mm, "end": v(-810, 193.5) * mm});
            skLineSegment(sketch, "E261.left", {"start": v(-630, -176.5) * mm, "end": v(-630, 193.5) * mm});
            skLineSegment(sketch, "E261.right", {"start": v(-810, -176.5) * mm, "end": v(-810, 193.5) * mm});
            skPoint(sketch, "E261.middle", {"position": v(-720, 8.5) * mm});
            skLineSegment(sketch, "E262.bottom", {"start": v(247, -176.5) * mm, "end": v(200, -176.5) * mm});
            skLineSegment(sketch, "E262.top", {"start": v(247, 193.5) * mm, "end": v(200, 193.5) * mm});
            skLineSegment(sketch, "E262.left", {"start": v(247, -176.5) * mm, "end": v(247, 193.5) * mm});
            skPoint(sketch, "E262.middle", {"position": v(223.5, 8.5) * mm});
            skLineSegment(sketch, "E263.trimOffspring", {"start": v(200, 193.5) * mm, "end": v(200, 327.5) * mm});
            skCircle(sketch, "E264", {"center": v(463.5, 192.5) * mm, "radius": 35 * mm});
            skCircle(sketch, "E265", {"center": v(-413.5, 192.5) * mm, "radius": 35 * mm});
            skCircle(sketch, "E266", {"center": v(-443.5, 317.5) * mm, "radius": 2.05 * mm});
            skCircle(sketch, "E267", {"center": v(-413.5, 317.5) * mm, "radius": 2.05 * mm});
            skCircle(sketch, "E268", {"center": v(-383.5, 317.5) * mm, "radius": 2.05 * mm});
            skCircle(sketch, "E269", {"center": v(433.5, 317.5) * mm, "radius": 2.05 * mm});
            skCircle(sketch, "E270", {"center": v(463.5, 317.5) * mm, "radius": 2.05 * mm});
            skCircle(sketch, "E271", {"center": v(493.5, 317.5) * mm, "radius": 2.05 * mm});
            skLineSegment(sketch, "E272.bottom", {"start": v(-383.5, 172.5) * mm, "end": v(-443.5, 172.5) * mm, "construction": true});
            skLineSegment(sketch, "E272.top", {"start": v(-383.5, 212.5) * mm, "end": v(-443.5, 212.5) * mm, "construction": true});
            skLineSegment(sketch, "E272.left", {"start": v(-378.5, 177.5) * mm, "end": v(-378.5, 207.5) * mm, "construction": true});
            skLineSegment(sketch, "E272.right", {"start": v(-448.5, 177.5) * mm, "end": v(-448.5, 207.5) * mm, "construction": true});
            skPoint(sketch, "E273.visualSharp", {"position": v(-448.5, 212.5) * mm});
            skArc(sketch, "E273.filletArc", {"start": v(-443.5, 212.5) * mm, "mid": v(-447.04, 211.04) * mm, "end": v(-448.5, 207.5) * mm, "construction": true});
            skPoint(sketch, "E274.visualSharp", {"position": v(-448.5, 172.5) * mm});
            skArc(sketch, "E274.filletArc", {"start": v(-448.5, 177.5) * mm, "mid": v(-447.04, 173.96) * mm, "end": v(-443.5, 172.5) * mm, "construction": true});
            skPoint(sketch, "E275.visualSharp", {"position": v(-378.5, 212.5) * mm});
            skArc(sketch, "E275.filletArc", {"start": v(-378.5, 207.5) * mm, "mid": v(-379.96, 211.04) * mm, "end": v(-383.5, 212.5) * mm, "construction": true});
            skPoint(sketch, "E276.visualSharp", {"position": v(-378.5, 172.5) * mm});
            skArc(sketch, "E276.filletArc", {"start": v(-383.5, 172.5) * mm, "mid": v(-379.96, 173.96) * mm, "end": v(-378.5, 177.5) * mm, "construction": true});
            skLineSegment(sketch, "E277.bottom", {"start": v(493.5, 172.5) * mm, "end": v(433.5, 172.5) * mm, "construction": true});
            skLineSegment(sketch, "E277.top", {"start": v(493.5, 212.5) * mm, "end": v(433.5, 212.5) * mm, "construction": true});
            skLineSegment(sketch, "E277.left", {"start": v(498.5, 177.5) * mm, "end": v(498.5, 207.5) * mm, "construction": true});
            skLineSegment(sketch, "E277.right", {"start": v(428.5, 177.5) * mm, "end": v(428.5, 207.5) * mm, "construction": true});
            skPoint(sketch, "E278.visualSharp", {"position": v(428.5, 212.5) * mm});
            skArc(sketch, "E278.filletArc", {"start": v(433.5, 212.5) * mm, "mid": v(429.96, 211.04) * mm, "end": v(428.5, 207.5) * mm, "construction": true});
            skPoint(sketch, "E279.visualSharp", {"position": v(428.5, 172.5) * mm});
            skArc(sketch, "E279.filletArc", {"start": v(428.5, 177.5) * mm, "mid": v(429.96, 173.96) * mm, "end": v(433.5, 172.5) * mm, "construction": true});
            skPoint(sketch, "E280.visualSharp", {"position": v(498.5, 212.5) * mm});
            skArc(sketch, "E280.filletArc", {"start": v(498.5, 207.5) * mm, "mid": v(497.04, 211.04) * mm, "end": v(493.5, 212.5) * mm, "construction": true});
            skPoint(sketch, "E281.visualSharp", {"position": v(498.5, 172.5) * mm});
            skArc(sketch, "E281.filletArc", {"start": v(493.5, 172.5) * mm, "mid": v(497.04, 173.96) * mm, "end": v(498.5, 177.5) * mm, "construction": true});
            skLineSegment(sketch, "E282.bottom", {"start": v(-995, -27.5) * mm, "end": v(-965, -27.5) * mm});
            skLineSegment(sketch, "E282.top", {"start": v(-995, 32.5) * mm, "end": v(-965, 32.5) * mm});
            skLineSegment(sketch, "E282.left", {"start": v(-995, -27.5) * mm, "end": v(-995, 32.5) * mm});
            skLineSegment(sketch, "E282.right", {"start": v(-965, -27.5) * mm, "end": v(-965, 32.5) * mm});
            skPoint(sketch, "E282.middle", {"position": v(-980, 2.5) * mm});
            skLineSegment(sketch, "E283.MirrorCS", {"start": v(965, -27.5) * mm, "end": v(965, 32.5) * mm});
            skPoint(sketch, "E284.MirrorP", {"position": v(980, 2.5) * mm});
            skLineSegment(sketch, "E285.MirrorCS", {"start": v(995, -27.5) * mm, "end": v(965, -27.5) * mm});
            skLineSegment(sketch, "E286.MirrorCS", {"start": v(995, -27.5) * mm, "end": v(995, 32.5) * mm});
            skLineSegment(sketch, "E287.MirrorCS", {"start": v(995, 32.5) * mm, "end": v(965, 32.5) * mm});
            skSolve(sketch);
        }
        {
            var Q0;
            Q0 = qSketchRegion(id + "F9", true);
            extrude(context, id + "F10", {"entities" : qUnion([Q0]), "depth" : 4.5 * mm, "offsetDistance" : 25 * mm});
        }
        {
            var Q0;
            Q0=qCreatedBy(makeId("Top.planeOp"),FACE);
            cPlane(context, id + "F11", {"entities" : qUnion([Q0]), "cplaneType" : CPlaneType.OFFSET, "offset" : 8.5 * mm, "width" : 150 * mm, "height" : 150 * mm});
        }
        {
            var Q0;
            Q0=makeQuery(id+"F1.opExtrude","SWEPT_EDGE",EDGE,{"disambiguationData":[OSD([sQuery(id+"F0.wireOp",EDGE,"E3.bottom"),sQuery(id+"F0.wireOp",EDGE,"E3.right")])]});
            var Q1;
            Q1=makeQuery(id+"F1.opExtrude","SWEPT_EDGE",EDGE,{"disambiguationData":[OSD([sQuery(id+"F0.wireOp",EDGE,"E3.bottom"),sQuery(id+"F0.wireOp",EDGE,"E3.left")])]});
            var Q2;
            Q2=makeQuery(id+"F1.opExtrude","SWEPT_EDGE",EDGE,{"disambiguationData":[OSD([sQuery(id+"F0.wireOp",EDGE,"E3.top"),sQuery(id+"F0.wireOp",EDGE,"E3.left")])]});
            var Q3;
            Q3=makeQuery(id+"F1.opExtrude","SWEPT_EDGE",EDGE,{"disambiguationData":[OSD([sQuery(id+"F0.wireOp",EDGE,"E3.top"),sQuery(id+"F0.wireOp",EDGE,"E3.right")])]});
            var Q4;
            Q4=makeQuery(id+"F6.opExtrude","SWEPT_EDGE",EDGE,{"disambiguationData":[OSD([sQuery(id+"F5.wireOp",EDGE,"E155.bottom"),sQuery(id+"F5.wireOp",EDGE,"E155.right")])]});
            var Q5;
            Q5=makeQuery(id+"F6.opExtrude","SWEPT_EDGE",EDGE,{"disambiguationData":[OSD([sQuery(id+"F5.wireOp",EDGE,"E155.bottom"),sQuery(id+"F5.wireOp",EDGE,"E155.left")])]});
            var Q6;
            Q6=makeQuery(id+"F6.opExtrude","SWEPT_EDGE",EDGE,{"disambiguationData":[OSD([sQuery(id+"F5.wireOp",EDGE,"E155.top"),sQuery(id+"F5.wireOp",EDGE,"E155.right")])]});
            var Q7;
            Q7=makeQuery(id+"F6.opExtrude","SWEPT_EDGE",EDGE,{"disambiguationData":[OSD([sQuery(id+"F5.wireOp",EDGE,"E155.top"),sQuery(id+"F5.wireOp",EDGE,"E155.left")])]});
            var Q8;
            Q8=makeQuery(id+"F8.opExtrude","SWEPT_EDGE",EDGE,{"disambiguationData":[OSD([sQuery(id+"F7.wireOp",EDGE,"E175.top"),sQuery(id+"F7.wireOp",EDGE,"E175.left")])]});
            var Q9;
            Q9=makeQuery(id+"F8.opExtrude","SWEPT_EDGE",EDGE,{"disambiguationData":[OSD([sQuery(id+"F7.wireOp",EDGE,"E175.top"),sQuery(id+"F7.wireOp",EDGE,"E175.right")])]});
            var Q10;
            Q10=makeQuery(id+"F8.opExtrude","SWEPT_EDGE",EDGE,{"disambiguationData":[OSD([sQuery(id+"F7.wireOp",EDGE,"E175.bottom"),sQuery(id+"F7.wireOp",EDGE,"E175.right")])]});
            var Q11;
            Q11=makeQuery(id+"F8.opExtrude","SWEPT_EDGE",EDGE,{"disambiguationData":[OSD([sQuery(id+"F7.wireOp",EDGE,"E175.bottom"),sQuery(id+"F7.wireOp",EDGE,"E175.left")])]});
            var Q12;
            Q12=makeQuery(id+"F8.opExtrude","SWEPT_EDGE",EDGE,{"disambiguationData":[OSD([sQuery(id+"F7.wireOp",EDGE,"E175.top"),sQuery(id+"F7.wireOp",EDGE,"E202")])]});
            var Q13;
            Q13=makeQuery(id+"F8.opExtrude","SWEPT_EDGE",EDGE,{"disambiguationData":[OSD([sQuery(id+"F7.wireOp",EDGE,"E175.top"),sQuery(id+"F7.wireOp",EDGE,"E200")])]});
            var Q14;
            Q14=makeQuery(id+"F8.opExtrude","SWEPT_EDGE",EDGE,{"disambiguationData":[OSD([sQuery(id+"F7.wireOp",EDGE,"E201"),sQuery(id+"F7.wireOp",EDGE,"E202")])]});
            var Q15;
            Q15=makeQuery(id+"F8.opExtrude","SWEPT_EDGE",EDGE,{"disambiguationData":[OSD([sQuery(id+"F7.wireOp",EDGE,"E200"),sQuery(id+"F7.wireOp",EDGE,"E201")])]});
            var Q16;
            Q16=makeQuery(id+"F10.opExtrude","SWEPT_EDGE",EDGE,{"disambiguationData":[OSD([sQuery(id+"F9.wireOp",EDGE,"E283.MirrorCS"),sQuery(id+"F9.wireOp",EDGE,"E287.MirrorCS")])]});
            var Q17;
            Q17=makeQuery(id+"F10.opExtrude","SWEPT_EDGE",EDGE,{"disambiguationData":[OSD([sQuery(id+"F9.wireOp",EDGE,"E283.MirrorCS"),sQuery(id+"F9.wireOp",EDGE,"E285.MirrorCS")])]});
            var Q18;
            Q18=makeQuery(id+"F10.opExtrude","SWEPT_EDGE",EDGE,{"disambiguationData":[OSD([sQuery(id+"F9.wireOp",EDGE,"E286.MirrorCS"),sQuery(id+"F9.wireOp",EDGE,"E287.MirrorCS")])]});
            var Q19;
            Q19=makeQuery(id+"F10.opExtrude","SWEPT_EDGE",EDGE,{"disambiguationData":[OSD([sQuery(id+"F9.wireOp",EDGE,"E285.MirrorCS"),sQuery(id+"F9.wireOp",EDGE,"E286.MirrorCS")])]});
            var Q20;
            Q20=makeQuery(id+"F10.opExtrude","SWEPT_EDGE",EDGE,{"disambiguationData":[OSD([sQuery(id+"F9.wireOp",EDGE,"E282.top"),sQuery(id+"F9.wireOp",EDGE,"E282.left")])]});
            var Q21;
            Q21=makeQuery(id+"F10.opExtrude","SWEPT_EDGE",EDGE,{"disambiguationData":[OSD([sQuery(id+"F9.wireOp",EDGE,"E282.top"),sQuery(id+"F9.wireOp",EDGE,"E282.right")])]});
            var Q22;
            Q22=makeQuery(id+"F10.opExtrude","SWEPT_EDGE",EDGE,{"disambiguationData":[OSD([sQuery(id+"F9.wireOp",EDGE,"E282.bottom"),sQuery(id+"F9.wireOp",EDGE,"E282.right")])]});
            var Q23;
            Q23=makeQuery(id+"F10.opExtrude","SWEPT_EDGE",EDGE,{"disambiguationData":[OSD([sQuery(id+"F9.wireOp",EDGE,"E282.bottom"),sQuery(id+"F9.wireOp",EDGE,"E282.left")])]});
            fillet(context, id + "F12", {"entities" : qUnion([Q0, Q1, Q2, Q3, Q4, Q5, Q6, Q7, Q8, Q9, Q10, Q11, Q12, Q13, Q14, Q15, Q16, Q17, Q18, Q19, Q20, Q21, Q22, Q23]), "radius" : 5 * mm, "tangentPropagation" : true, "defaultsChanged" : false, "vertexSettings" : [], "allowEdgeOverflow" : false});
        }
        {
            var Q0;
            Q0=qCreatedBy(makeId("Top.planeOp"),FACE);
            var sketch = newSketch(context, id + "F13", { "sketchPlane" : qUnion([Q0])});
            skLineSegment(sketch, "E288.bottom", {"start": v(-200, -982.5) * mm, "end": v(-1010, -982.5) * mm});
            skLineSegment(sketch, "E288.top", {"start": v(-200, -327.5) * mm, "end": v(-1010, -327.5) * mm});
            skLineSegment(sketch, "E288.left", {"start": v(-200, -982.5) * mm, "end": v(-200, -327.5) * mm});
            skLineSegment(sketch, "E288.right", {"start": v(-1010, -982.5) * mm, "end": v(-1010, -327.5) * mm});
            skPoint(sketch, "E288.middle", {"position": v(-605, -655) * mm});
            skLineSegment(sketch, "E289", {"start": v(0, 0) * mm, "end": v(0, -943.44) * mm, "construction": true});
            skLineSegment(sketch, "E290.MirrorCS", {"start": v(200, -327.5) * mm, "end": v(1010, -327.5) * mm});
            skLineSegment(sketch, "E291.MirrorCS", {"start": v(200, -982.5) * mm, "end": v(1010, -982.5) * mm});
            skLineSegment(sketch, "E292.MirrorCS", {"start": v(200, -982.5) * mm, "end": v(200, -327.5) * mm});
            skLineSegment(sketch, "E293.MirrorCS", {"start": v(1010, -982.5) * mm, "end": v(1010, -327.5) * mm});
            skPoint(sketch, "E294.MirrorP", {"position": v(605, -655) * mm});
            skCircle(sketch, "E295", {"center": v(-930, -342.5) * mm, "radius": 3 * mm});
            skCircle(sketch, "E296", {"center": v(-900, -342.5) * mm, "radius": 3 * mm});
            skCircle(sketch, "E297", {"center": v(-215, -342.5) * mm, "radius": 3 * mm});
            skCircle(sketch, "E298", {"center": v(-930, -967.5) * mm, "radius": 3 * mm});
            skCircle(sketch, "E299", {"center": v(-900, -967.5) * mm, "radius": 3 * mm});
            skCircle(sketch, "E300", {"center": v(-215, -967.5) * mm, "radius": 3 * mm});
            skCircle(sketch, "E301.MirrorC", {"center": v(215, -967.5) * mm, "radius": 3 * mm});
            skCircle(sketch, "E302.MirrorC", {"center": v(930, -967.5) * mm, "radius": 3 * mm});
            skCircle(sketch, "E303.MirrorC", {"center": v(900, -967.5) * mm, "radius": 3 * mm});
            skCircle(sketch, "E304.MirrorC", {"center": v(215, -342.5) * mm, "radius": 3 * mm});
            skCircle(sketch, "E305.MirrorC", {"center": v(930, -342.5) * mm, "radius": 3 * mm});
            skCircle(sketch, "E306.MirrorC", {"center": v(900, -342.5) * mm, "radius": 3 * mm});
            skSolve(sketch);
        }
        {
            var Q0;
            Q0 = qSketchRegion(id + "F13", true);
            extrude(context, id + "F14", {"entities" : qUnion([Q0]), "depth" : 4.5 * mm, "offsetDistance" : 25 * mm});
        }
        {
            var Q0;
            Q0=qCreatedBy(makeId("Top.planeOp"),FACE);
            var sketch = newSketch(context, id + "F15", { "sketchPlane" : qUnion([Q0])});
            skLineSegment(sketch, "E307.bottom", {"start": v(200, -982.5) * mm, "end": v(-200, -982.5) * mm});
            skLineSegment(sketch, "E307.top", {"start": v(200, -327.5) * mm, "end": v(-200, -327.5) * mm});
            skLineSegment(sketch, "E307.left", {"start": v(200, -982.5) * mm, "end": v(200, -327.5) * mm});
            skLineSegment(sketch, "E307.right", {"start": v(-200, -982.5) * mm, "end": v(-200, -327.5) * mm});
            skPoint(sketch, "E307.middle", {"position": v(0, -655) * mm});
            skCircle(sketch, "E308", {"center": v(-185, -342.5) * mm, "radius": 3 * mm});
            skCircle(sketch, "E309", {"center": v(185, -342.5) * mm, "radius": 3 * mm});
            skCircle(sketch, "E310", {"center": v(-185, -967.5) * mm, "radius": 3 * mm});
            skCircle(sketch, "E311", {"center": v(185, -967.5) * mm, "radius": 3 * mm});
            skSolve(sketch);
        }
        {
            var Q0;
            Q0 = qSketchRegion(id + "F15", true);
            extrude(context, id + "F16", {"entities" : qUnion([Q0]), "depth" : 4.5 * mm, "offsetDistance" : 25 * mm});
        }
        {
            var Q0;
            Q0=qCreatedBy(makeId("Top.planeOp"),FACE);
            var sketch = newSketch(context, id + "F17", { "sketchPlane" : qUnion([Q0])});
            skLineSegment(sketch, "E312.bottom", {"start": v(-1010, -1665.5) * mm, "end": v(-200, -1665.5) * mm});
            skLineSegment(sketch, "E312.top", {"start": v(-1010, -982.5) * mm, "end": v(-200, -982.5) * mm});
            skLineSegment(sketch, "E312.left", {"start": v(-1010, -1665.5) * mm, "end": v(-1010, -982.5) * mm});
            skLineSegment(sketch, "E312.right", {"start": v(-200, -1665.5) * mm, "end": v(-200, -982.5) * mm});
            skLineSegment(sketch, "E313", {"start": v(0, -1840) * mm, "end": v(0, -1176.64) * mm, "construction": true});
            skCircle(sketch, "E314", {"center": v(-930, -997.5) * mm, "radius": 3 * mm});
            skCircle(sketch, "E315", {"center": v(-900, -997.5) * mm, "radius": 3 * mm});
            skCircle(sketch, "E316", {"center": v(-215, -997.5) * mm, "radius": 3 * mm});
            skCircle(sketch, "E317", {"center": v(-930, -1635.5) * mm, "radius": 3 * mm});
            skCircle(sketch, "E318", {"center": v(-900, -1635.5) * mm, "radius": 3 * mm});
            skCircle(sketch, "E319", {"center": v(-930, -1605.5) * mm, "radius": 3 * mm});
            skCircle(sketch, "E320", {"center": v(-900, -1605.5) * mm, "radius": 3 * mm});
            skCircle(sketch, "E321", {"center": v(-215, -1635.5) * mm, "radius": 3 * mm});
            skCircle(sketch, "E322", {"center": v(-215, -1605.5) * mm, "radius": 3 * mm});
            skCircle(sketch, "E323.MirrorC", {"center": v(215, -997.5) * mm, "radius": 3 * mm});
            skCircle(sketch, "E324.MirrorC", {"center": v(930, -1635.5) * mm, "radius": 3 * mm});
            skCircle(sketch, "E325.MirrorC", {"center": v(900, -1605.5) * mm, "radius": 3 * mm});
            skCircle(sketch, "E326.MirrorC", {"center": v(930, -997.5) * mm, "radius": 3 * mm});
            skCircle(sketch, "E327.MirrorC", {"center": v(215, -1605.5) * mm, "radius": 3 * mm});
            skCircle(sketch, "E328.MirrorC", {"center": v(900, -1635.5) * mm, "radius": 3 * mm});
            skCircle(sketch, "E329.MirrorC", {"center": v(930, -1605.5) * mm, "radius": 3 * mm});
            skCircle(sketch, "E330.MirrorC", {"center": v(900, -997.5) * mm, "radius": 3 * mm});
            skCircle(sketch, "E331.MirrorC", {"center": v(215, -1635.5) * mm, "radius": 3 * mm});
            skLineSegment(sketch, "E332.MirrorCS", {"start": v(1010, -1665.5) * mm, "end": v(1010, -982.5) * mm});
            skLineSegment(sketch, "E333.MirrorCS", {"start": v(200, -1665.5) * mm, "end": v(200, -982.5) * mm});
            skLineSegment(sketch, "E334.MirrorCS", {"start": v(1010, -982.5) * mm, "end": v(200, -982.5) * mm});
            skLineSegment(sketch, "E335.MirrorCS", {"start": v(1010, -1665.5) * mm, "end": v(200, -1665.5) * mm});
            skLineSegment(sketch, "E336.bottom", {"start": v(960, -1415.5) * mm, "end": v(560, -1415.5) * mm, "construction": true});
            skLineSegment(sketch, "E336.top", {"start": v(960, -815.5) * mm, "end": v(560, -815.5) * mm, "construction": true});
            skLineSegment(sketch, "E336.left", {"start": v(960, -1415.5) * mm, "end": v(960, -815.5) * mm, "construction": true});
            skLineSegment(sketch, "E336.right", {"start": v(560, -1415.5) * mm, "end": v(560, -815.5) * mm, "construction": true});
            skPoint(sketch, "E336.middle", {"position": v(760, -1115.5) * mm});
            skCircle(sketch, "E337", {"center": v(760, -1115.5) * mm, "radius": 35 * mm});
            skSolve(sketch);
        }
        {
            var Q0;
            Q0 = qSketchRegion(id + "F17", true);
            extrude(context, id + "F18", {"entities" : qUnion([Q0]), "depth" : 4.5 * mm, "offsetDistance" : 25 * mm});
        }
        {
            var Q0;
            Q0=qCreatedBy(makeId("Top.planeOp"),FACE);
            var sketch = newSketch(context, id + "F19", { "sketchPlane" : qUnion([Q0])});
            skLineSegment(sketch, "E338.bottom", {"start": v(-200, -1665.5) * mm, "end": v(200, -1665.5) * mm});
            skLineSegment(sketch, "E338.top", {"start": v(-200, -982.5) * mm, "end": v(200, -982.5) * mm});
            skLineSegment(sketch, "E338.left", {"start": v(-200, -1665.5) * mm, "end": v(-200, -982.5) * mm});
            skLineSegment(sketch, "E338.right", {"start": v(200, -1665.5) * mm, "end": v(200, -982.5) * mm});
            skCircle(sketch, "E339", {"center": v(-185, -997.5) * mm, "radius": 3 * mm});
            skCircle(sketch, "E340", {"center": v(-185, -1635.5) * mm, "radius": 3 * mm});
            skCircle(sketch, "E341", {"center": v(-185, -1605.5) * mm, "radius": 3 * mm});
            skLineSegment(sketch, "E342", {"start": v(0, -1180.39) * mm, "end": v(0, -1421.36) * mm, "construction": true});
            skCircle(sketch, "E343.MirrorC", {"center": v(185, -997.5) * mm, "radius": 3 * mm});
            skCircle(sketch, "E344.MirrorC", {"center": v(185, -1635.5) * mm, "radius": 3 * mm});
            skCircle(sketch, "E345.MirrorC", {"center": v(185, -1605.5) * mm, "radius": 3 * mm});
            skSolve(sketch);
        }
        {
            var Q0;
            Q0 = qSketchRegion(id + "F19", true);
            extrude(context, id + "F20", {"entities" : qUnion([Q0]), "depth" : 4.5 * mm, "offsetDistance" : 25 * mm});
        }
        {
            var Q0;
            Q0=qCreatedBy(id+"F11.planeOp",FACE);
            var sketch = newSketch(context, id + "F21", { "sketchPlane" : qUnion([Q0])});
            skLineSegment(sketch, "E346.bottom", {"start": v(-1218.22, 328) * mm, "end": v(1275.22, 328) * mm});
            skLineSegment(sketch, "E346.top", {"start": v(-1218.22, 327) * mm, "end": v(1275.22, 327) * mm});
            skLineSegment(sketch, "E346.left", {"start": v(-1218.22, 328) * mm, "end": v(-1218.22, 327) * mm});
            skLineSegment(sketch, "E346.right", {"start": v(1275.22, 328) * mm, "end": v(1275.22, 327) * mm});
            skLineSegment(sketch, "E347.bottom", {"start": v(-1136.47, 878) * mm, "end": v(1063.53, 878) * mm});
            skLineSegment(sketch, "E347.top", {"start": v(-1136.47, 877) * mm, "end": v(1063.53, 877) * mm});
            skLineSegment(sketch, "E347.left", {"start": v(-1136.47, 878) * mm, "end": v(-1136.47, 877) * mm});
            skLineSegment(sketch, "E347.right", {"start": v(1063.53, 878) * mm, "end": v(1063.53, 877) * mm});
            skLineSegment(sketch, "E348.bottom", {"start": v(-200.5, 1674.84) * mm, "end": v(-199.5, 1674.84) * mm});
            skLineSegment(sketch, "E348.top", {"start": v(-200.5, -1825.16) * mm, "end": v(-199.5, -1825.16) * mm});
            skLineSegment(sketch, "E348.left", {"start": v(-200.5, 1674.84) * mm, "end": v(-200.5, -1825.16) * mm});
            skLineSegment(sketch, "E348.right", {"start": v(-199.5, 1674.84) * mm, "end": v(-199.5, -1825.16) * mm});
            skLineSegment(sketch, "E349.bottom", {"start": v(199.5, 1674.84) * mm, "end": v(200.5, 1674.84) * mm});
            skLineSegment(sketch, "E349.top", {"start": v(199.5, -1825.16) * mm, "end": v(200.5, -1825.16) * mm});
            skLineSegment(sketch, "E349.left", {"start": v(199.5, 1674.84) * mm, "end": v(199.5, -1825.16) * mm});
            skLineSegment(sketch, "E349.right", {"start": v(200.5, 1674.84) * mm, "end": v(200.5, -1825.16) * mm});
            skLineSegment(sketch, "E350.bottom", {"start": v(-1492.65, -327) * mm, "end": v(1026.9, -327) * mm});
            skLineSegment(sketch, "E350.top", {"start": v(-1492.65, -328) * mm, "end": v(1026.9, -328) * mm});
            skLineSegment(sketch, "E350.left", {"start": v(-1492.65, -327) * mm, "end": v(-1492.65, -328) * mm});
            skLineSegment(sketch, "E350.right", {"start": v(1026.9, -327) * mm, "end": v(1026.9, -328) * mm});
            skLineSegment(sketch, "E351.bottom", {"start": v(-1075.1, -983) * mm, "end": v(1070.3, -983) * mm});
            skLineSegment(sketch, "E351.top", {"start": v(-1075.1, -982) * mm, "end": v(1070.3, -982) * mm});
            skLineSegment(sketch, "E351.left", {"start": v(-1075.1, -983) * mm, "end": v(-1075.1, -982) * mm});
            skLineSegment(sketch, "E351.right", {"start": v(1070.3, -983) * mm, "end": v(1070.3, -982) * mm});
            skSolve(sketch);
        }
        {
            var Q0;
            Q0 = qSketchRegion(id + "F21", true);
            var Q1;
            {var subQ0=sQuery(id+"F21.wireOp",EDGE,"E350.bottom");var subQ1=sQuery(id+"F21.wireOp",EDGE,"E348.right");var subQ2=makeQuery(id+"F21.imprint","INTERSECT",VERTEX,{"derivedFrom":[subQ1,subQ0]});Q1=makeQuery(id+"F21.imprint","IMPRINT",FACE,{"disambiguationData":[TD([[makeQuery(id+"F21.imprint","IMPRINT",EDGE,{"disambiguationData":[TD([[subQ2,-1.0]])],"derivedFrom":subQ1}),1.0]])]});}
            var Q2;
            {var subQ0=sQuery(id+"F21.wireOp",EDGE,"E348.right");var subQ1=sQuery(id+"F21.wireOp",EDGE,"E346.bottom");var subQ2=makeQuery(id+"F21.imprint","INTERSECT",VERTEX,{"derivedFrom":[subQ1,subQ0]});Q2=makeQuery(id+"F21.imprint","IMPRINT",FACE,{"disambiguationData":[TD([[makeQuery(id+"F21.imprint","IMPRINT",EDGE,{"disambiguationData":[TD([[subQ2,-1.0]])],"derivedFrom":subQ1}),-1.0]])]});}
            extrude(context, id + "F22", {"entities" : qUnion([Q0, Q1, Q2]), "operationType" : NewBodyOperationType.REMOVE, "endBound" : BoundingType.THROUGH_ALL, "oppositeDirection" : true, "depth" : 25 * mm, "offsetDistance" : 25 * mm});
        }
    });
